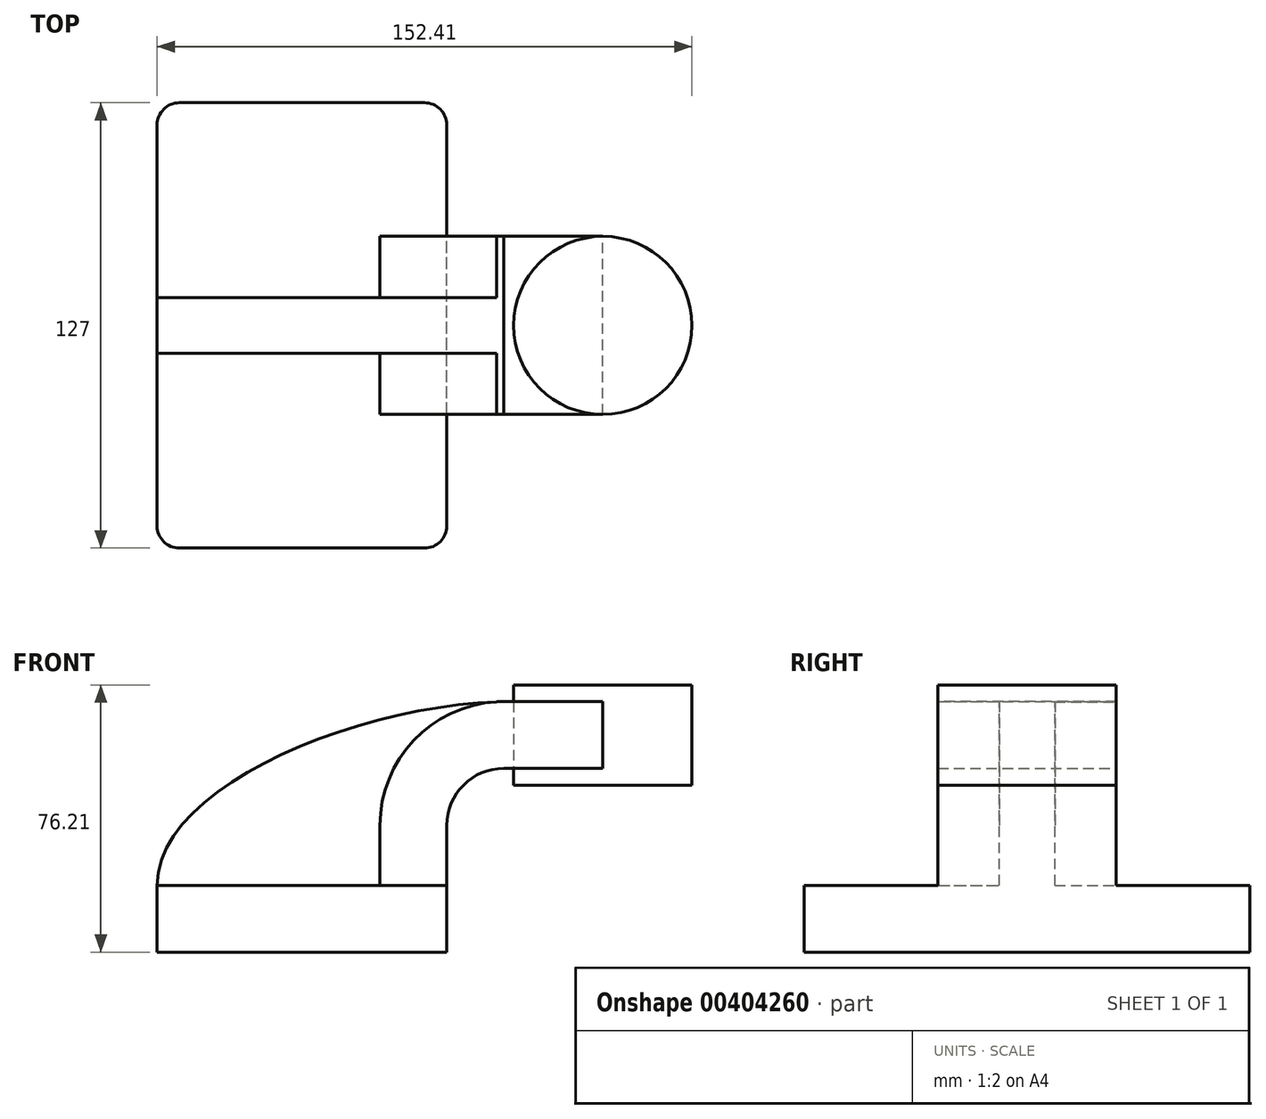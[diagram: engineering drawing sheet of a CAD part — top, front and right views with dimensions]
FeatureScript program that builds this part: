
annotation { "Feature Type Name" : "Feature", "Feature Type Description" : "" }
export const myFeature = defineFeature(function(context is Context, id is Id, definition is map)
    precondition{}
    {
        {
            var Q0;
            Q0=qCreatedBy(makeId("Front.planeOp"),FACE);
            var sketch = newSketch(context, id + "F0", { "sketchPlane" : qUnion([Q0])});
            skLineSegment(sketch, "E0.bottom", {"start": v(-41.28, 9.52) * mm, "end": v(41.27, 9.53) * mm});
            skLineSegment(sketch, "E0.top", {"start": v(-41.28, -9.53) * mm, "end": v(41.28, -9.53) * mm});
            skLineSegment(sketch, "E0.left", {"start": v(-41.28, 9.52) * mm, "end": v(-41.27, -9.53) * mm});
            skLineSegment(sketch, "E0.right", {"start": v(41.28, 9.53) * mm, "end": v(41.28, -9.52) * mm});
            skPoint(sketch, "E0.middle", {"position": v(0, 0) * mm});
            skLineSegment(sketch, "E1.bottom", {"start": v(60.32, 38.1) * mm, "end": v(111.12, 38.1) * mm});
            skLineSegment(sketch, "E1.top", {"start": v(60.32, 66.68) * mm, "end": v(111.12, 66.68) * mm});
            skLineSegment(sketch, "E1.left", {"start": v(60.32, 38.1) * mm, "end": v(60.32, 66.68) * mm});
            skLineSegment(sketch, "E1.right", {"start": v(111.12, 38.1) * mm, "end": v(111.12, 66.68) * mm});
            skPoint(sketch, "E1.middle", {"position": v(85.72, 52.39) * mm});
            skLineSegment(sketch, "E2", {"start": v(41.27, 9.53) * mm, "end": v(41.27, 26.6) * mm});
            skArc(sketch, "E3", {"start": v(41.27, 26.6) * mm, "mid": v(46.04, 38.1) * mm, "end": v(57.53, 42.86) * mm});
            skLineSegment(sketch, "E4", {"start": v(57.53, 42.86) * mm, "end": v(85.72, 42.86) * mm});
            skLineSegment(sketch, "E5.0", {"start": v(57.53, 61.91) * mm, "end": v(85.72, 61.91) * mm});
            skArc(sketch, "E5.1", {"start": v(22.22, 26.6) * mm, "mid": v(32.57, 51.57) * mm, "end": v(57.53, 61.91) * mm});
            skLineSegment(sketch, "E5.2", {"start": v(22.22, 9.53) * mm, "end": v(22.22, 26.6) * mm});
            skLineSegment(sketch, "E6", {"start": v(85.72, 38.1) * mm, "end": v(85.72, 61.91) * mm});
            skFitSpline(sketch, "E7", {"points": [v(-41.28, 9.53) * mm, v(57.53, 61.91) * mm], "startDerivative": vector(-0.27, 84.77) * mm, "endDerivative": vector(124.3, 2.47) * mm});
            skLineSegment(sketch, "E8", {"start": v(85.72, 38.1) * mm, "end": v(85.72, 66.68) * mm});
            skSolve(sketch);
        }
        {
            var Q0;
            Q0=makeQuery(id+"F0.imprint","IMPRINT",FACE,{"disambiguationData":[TD([[makeQuery(id+"F0.imprint","IMPRINT",EDGE,{"derivedFrom":sQuery(id+"F0.wireOp",EDGE,"E0.top")}),1.0]])]});
            extrude(context, id + "F1", {"entities" : qUnion([Q0]), "endBound" : BoundingType.SYMMETRIC, "depth" : 127 * mm});
        }
        {
            var Q0;
            {var subQ6=sQuery(id+"F0.wireOp",EDGE,"E2");Q0=makeQuery(id+"F0.imprint","IMPRINT",FACE,{"disambiguationData":[TD([[makeQuery(id+"F0.imprint","IMPRINT",EDGE,{"derivedFrom":subQ6}),1.0]])]});}
            var Q1;
            {var subQ0=sQuery(id+"F0.wireOp",EDGE,"E4");var subQ1=sQuery(id+"F0.wireOp",EDGE,"E1.left");var subQ2=makeQuery(id+"F0.imprint","INTERSECT",VERTEX,{"derivedFrom":[subQ1,subQ0]});Q1=makeQuery(id+"F0.imprint","IMPRINT",FACE,{"disambiguationData":[TD([[makeQuery(id+"F0.imprint","IMPRINT",EDGE,{"disambiguationData":[TD([[subQ2,-1.0]])],"derivedFrom":subQ1}),-1.0]])]});}
            extrude(context, id + "F2", {"entities" : qUnion([Q0, Q1]), "operationType" : NewBodyOperationType.ADD, "endBound" : BoundingType.SYMMETRIC, "depth" : 50.8 * mm});
        }
        {
            var Q0;
            {var subQ3=sQuery(id+"F0.wireOp",EDGE,"E5.2");Q0=makeQuery(id+"F0.imprint","IMPRINT",FACE,{"disambiguationData":[TD([[makeQuery(id+"F0.imprint","IMPRINT",EDGE,{"derivedFrom":subQ3}),1.0]])]});}
            extrude(context, id + "F3", {"entities" : qUnion([Q0]), "operationType" : NewBodyOperationType.ADD, "endBound" : BoundingType.SYMMETRIC, "depth" : 15.88 * mm});
        }
        {
            var Q0;
            {var subQ4=sQuery(id+"F0.wireOp",EDGE,"E1.right");Q0=makeQuery(id+"F0.imprint","IMPRINT",FACE,{"disambiguationData":[TD([[makeQuery(id+"F0.imprint","IMPRINT",EDGE,{"derivedFrom":subQ4}),1.0]])]});}
            var Q1;
            Q1=sQuery(id+"F0.wireOp",EDGE,"E8");
            revolve(context, id + "F4", {"entities" : qUnion([Q0]), "axis" : qUnion([Q1]), "revolveType" : RevolveType.FULL});
        }
        {
            var Q0;
            Q0=makeQuery(id+"F1.opExtrude","CAP_EDGE",EDGE,{"disambiguationData":[OSD([sQuery(id+"F0.wireOp",EDGE,"E0.left")])],"isStart":false});
            var Q1;
            Q1=makeQuery(id+"F1.opExtrude","CAP_EDGE",EDGE,{"disambiguationData":[OSD([sQuery(id+"F0.wireOp",EDGE,"E0.right")])],"isStart":false});
            var Q2;
            Q2=makeQuery(id+"F1.opExtrude","CAP_EDGE",EDGE,{"disambiguationData":[OSD([sQuery(id+"F0.wireOp",EDGE,"E0.right")])],"isStart":true});
            var Q3;
            Q3=makeQuery(id+"F1.opExtrude","CAP_EDGE",EDGE,{"disambiguationData":[OSD([sQuery(id+"F0.wireOp",EDGE,"E0.left")])],"isStart":true});
            fillet(context, id + "F5", {"entities" : qUnion([Q0, Q1, Q2, Q3]), "radius" : 6.35 * mm, "tangentPropagation" : true, "allowEdgeOverflow" : false});
        }
    });
